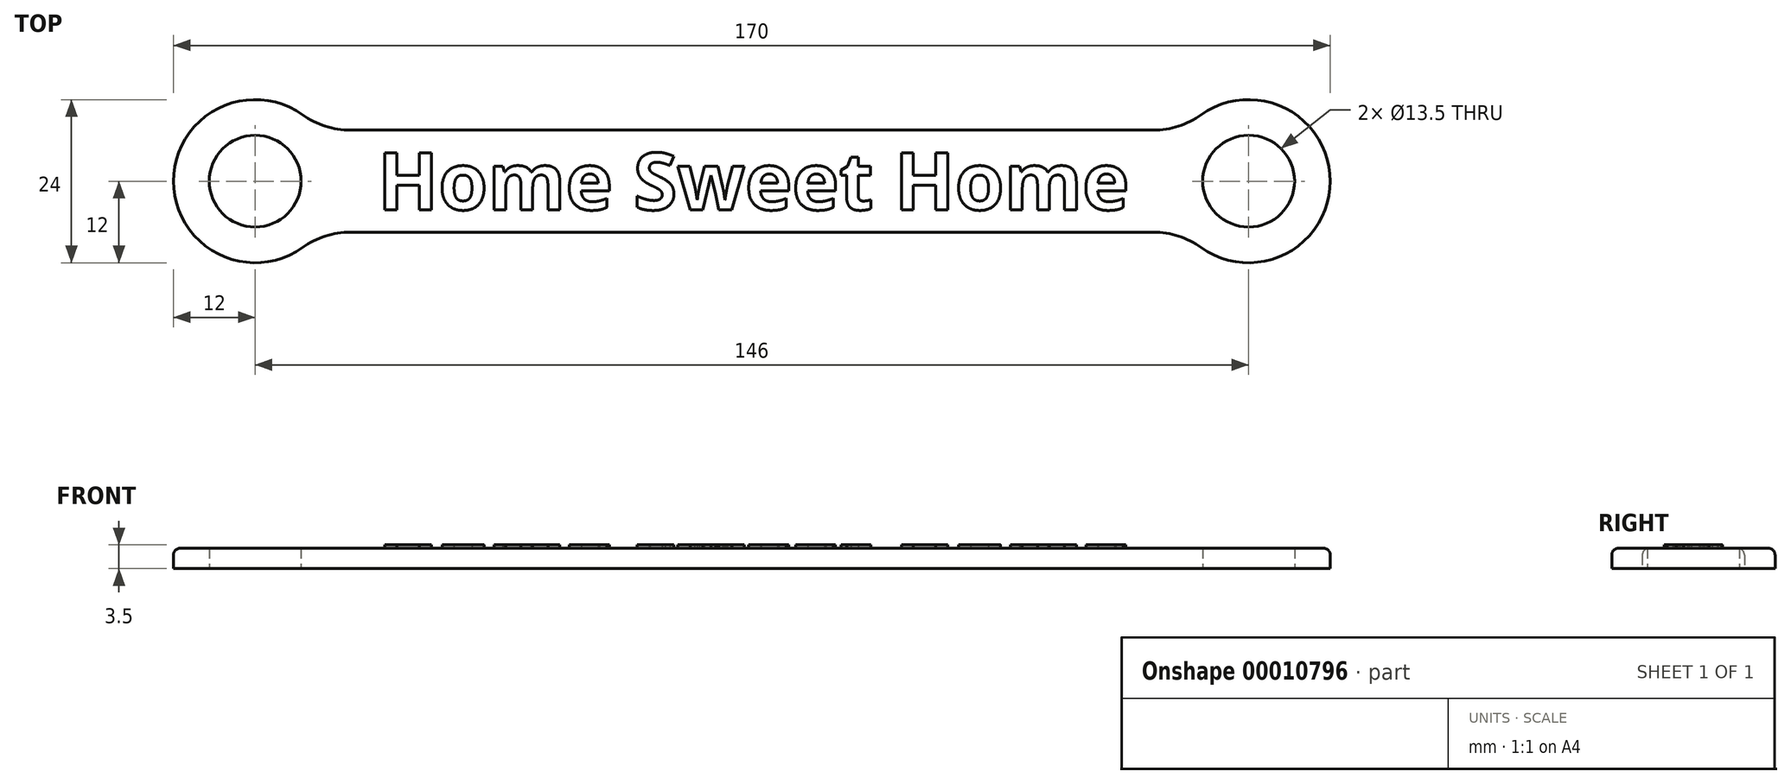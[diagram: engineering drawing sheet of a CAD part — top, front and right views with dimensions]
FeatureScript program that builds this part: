
annotation { "Feature Type Name" : "Feature", "Feature Type Description" : "" }
export const myFeature = defineFeature(function(context is Context, id is Id, definition is map)
    precondition{}
    {
        {
            var Q0;
            Q0=qCreatedBy(makeId("Top.planeOp"),FACE);
            var sketch = newSketch(context, id + "F0", { "sketchPlane" : qUnion([Q0])});
            skCircle(sketch, "E0", {"center": v(-73, 0) * mm, "radius": 6.75 * mm});
            skArc(sketch, "E1", {"start": v(-66, 9.75) * mm, "mid": v(-85, 0) * mm, "end": v(-66, -9.75) * mm});
            skLineSegment(sketch, "E2", {"start": v(0, 7.5) * mm, "end": v(-59, 7.5) * mm});
            skLineSegment(sketch, "E3", {"start": v(-59, -7.5) * mm, "end": v(0, -7.5) * mm});
            skLineSegment(sketch, "E4", {"start": v(-73, 0) * mm, "end": v(0, 0) * mm, "construction": true});
            skLineSegment(sketch, "E5", {"start": v(0, 0) * mm, "end": v(0, 32.48) * mm, "construction": true});
            skPoint(sketch, "E6.visualSharp", {"position": v(-63.63, 7.5) * mm});
            skArc(sketch, "E6.filletArc", {"start": v(-66, 9.75) * mm, "mid": v(-62.68, 8.08) * mm, "end": v(-59, 7.5) * mm});
            skPoint(sketch, "E7.visualSharp", {"position": v(-63.63, -7.5) * mm});
            skArc(sketch, "E7.filletArc", {"start": v(-59, -7.5) * mm, "mid": v(-62.68, -8.08) * mm, "end": v(-66, -9.75) * mm});
            skLineSegment(sketch, "E8.0.MirrorCS", {"start": v(0, 7.5) * mm, "end": v(59, 7.5) * mm});
            skLineSegment(sketch, "E9.0.MirrorCS", {"start": v(59, -7.5) * mm, "end": v(0, -7.5) * mm});
            skArc(sketch, "E10.0.MirrorCS", {"start": v(59, -7.5) * mm, "mid": v(62.68, -8.08) * mm, "end": v(66, -9.75) * mm});
            skArc(sketch, "E11.0.MirrorCS", {"start": v(66, 9.75) * mm, "mid": v(62.68, 8.08) * mm, "end": v(59, 7.5) * mm});
            skArc(sketch, "E12.0.MirrorCS", {"start": v(66, 9.75) * mm, "mid": v(85, 0) * mm, "end": v(66, -9.75) * mm});
            skCircle(sketch, "E13.0.MirrorC", {"center": v(73, 0) * mm, "radius": 6.75 * mm});
            skLineSegment(sketch, "E14", {"start": v(-89.97, 0) * mm, "end": v(0, 89.97) * mm, "construction": true});
            skLineSegment(sketch, "E15", {"start": v(0, 89.97) * mm, "end": v(89.97, 0) * mm, "construction": true});
            skLineSegment(sketch, "E16", {"start": v(89.97, 0) * mm, "end": v(0, -89.97) * mm, "construction": true});
            skLineSegment(sketch, "E17", {"start": v(0, -89.97) * mm, "end": v(-89.97, 0) * mm, "construction": true});
            skSolve(sketch);
        }
        {
            var Q0;
            Q0=qSketchRegion(id+"F0",true);
            extrude(context, id + "F1", {"entities" : qUnion([Q0]), "depth" : 3 * mm});
        }
        {
            var Q0;
            Q0=makeQuery(id+"F1.opExtrude","CAP_EDGE",EDGE,{"disambiguationData":[OSD([sQuery(id+"F0.wireOp",EDGE,"E3"),sQuery(id+"F0.wireOp",EDGE,"E9.0.MirrorCS")])],"isStart":false});
            fillet(context, id + "F2", {"entities" : qUnion([Q0]), "radius" : 1 * mm, "tangentPropagation" : true, "allowEdgeOverflow" : false});
        }
        {
            var Q0;
            Q0=makeQuery(id+"F1.opExtrude","CAP_FACE",FACE,{"disambiguationData":[OSD([sQuery(id+"F0.wireOp",EDGE,"E0"),sQuery(id+"F0.wireOp",EDGE,"E1"),sQuery(id+"F0.wireOp",EDGE,"E2"),sQuery(id+"F0.wireOp",EDGE,"E3"),sQuery(id+"F0.wireOp",EDGE,"E6.filletArc"),sQuery(id+"F0.wireOp",EDGE,"E7.filletArc"),sQuery(id+"F0.wireOp",EDGE,"E8.0.MirrorCS"),sQuery(id+"F0.wireOp",EDGE,"E9.0.MirrorCS"),sQuery(id+"F0.wireOp",EDGE,"E10.0.MirrorCS"),sQuery(id+"F0.wireOp",EDGE,"E11.0.MirrorCS"),sQuery(id+"F0.wireOp",EDGE,"E12.0.MirrorCS"),sQuery(id+"F0.wireOp",EDGE,"E13.0.MirrorC")])],"isStart":false});
            var sketch = newSketch(context, id + "F3", { "sketchPlane" : qUnion([Q0])});
            skText(sketch, "E18", { "text": "Home Sweet Home", "fontName": "OpenSans-Bold.ttf"});
            skLineSegment(sketch, "E19", {"start": v(0, 33.52) * mm, "end": v(0, 0) * mm, "construction": true});
            skLineSegment(sketch, "E20", {"start": v(0, 0) * mm, "end": v(89.81, 0) * mm, "construction": true});
            const initialGuessF3  = {"E18": [-0.055, -0.0042, 1, 0, 0.00841]};
            skSetInitialGuess(sketch, initialGuessF3);
            skSolve(sketch);
        }
        {
            var Q0;
            Q0 = qSketchRegion(id + "F3", true);
            extrude(context, id + "F4", {"entities" : qUnion([Q0]), "operationType" : NewBodyOperationType.ADD, "depth" : 0.5 * mm});
        }
    });
